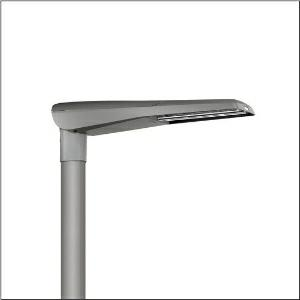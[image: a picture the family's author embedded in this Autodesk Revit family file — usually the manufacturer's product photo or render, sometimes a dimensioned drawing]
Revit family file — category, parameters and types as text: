
# Revit family: streetlight_sl_11_iq_mini___st1_0ab_5xc2nc1f08ge_aec6
name_source: partatom
category: Lighting Fixtures
units: mm (PartAtom-declared; Revit-internal decimal feet)

## family parameters
Cut with Voids When Loaded = No
Host = Face
Light Source = No
Part Type = Normal
Room Calculation Point = No
Round Connector Dimension = Use Diameter
Shared = No

## types (1)
- --- (1 x LED, 2430 lm, 25.3 W, 2200K)
    Apparent Load = 25 VA
    CIE Flux Codes = 29 63 95 100 100
    Color Rendering = 70
    Color Temperature = 2200K
    Default Elevation = 1800 mm
    Description = Streetlight SL 11 iQ mini, mast luminaire, primary light control with 3 zone facetted reflector, of plastic, silver coated, highly specular, primary optical cover: cover, of PMMA, transparent, light distribution: ST1.0aB, light emission: direct distribution, primary light characteristic: asymmetric, installation type: post-top, side-entry, LED, High Power LED, rated luminous flux: 3.010lm, luminous efficacy: 121lm/W, light colour: 722/727/730/740, colour temperature: 2200/2700/3000/4000K, control gear: iQ Street-Remote, control: Street-Remote, Auto-Match, Temp-Guard, Lumen-Switch, Night-Set, Smart-Wire, Light-Fading, Desk-Remote (wireless, voltage-free reading and setting of iQ features in the workshop via application-optimized NFC function/RFID function), optimised constant luminous flux control (CLO 2.0), with cable H07RN-F 5x 1.5mm², mains connection: 230..240V, AC, 50/60Hz, connection cable pre-assembled, cable length: 6,5m, start of lifetime: 25W, end of service life: 26W, reduction: 13W, luminaire housing, of diecast aluminium, powder-coated, Siteco® metallic grey (DB 702S), please order mast flange separately, inclination adjustable without tools: 0°, 5°, 10°, 15° (post-top) | 0°, -5°, -10°, -15° (side-entry), sealing non-destructively replaceable, multi-level sealing system, length: 736mm, width: 174mm, height: 116mm, mast flange for spigot size: 42mm (side-entry): 5XC10008XM4, 60/48mm (side-entry/post-top): 5XC10108XM2, 76/60mm (side-entry/post-top): 5XC10108XM1, mounting height: 4..8m, equipment: standard, protection rating (complete): IP66, insulation class (complete): insulation class II (safety insulation), certification: CE, ENEC, VDE, impact resistance: IK09, permissible operating ambient temperature for outdoor applications: -25..+50°C, standard-compliant lighting for roads and squares, Environmental Product Declaration (EPD) tested and certified by an independent institute, packaging unit: 1 piece

Light Distribution: ST1.0aB
    Height = 116 mm
    Lamp = 1 x LED
    Lamp Light Flux = 2430 lm
    Lamp Power = 25.3 W
    Lamp count = 1
    Length = 736 mm
    Luminous efficacy = 96 lm/W
    Manufacturer = Siteco
    ModVariant = No
    Model = 5XC2NC1F08GE
    Number of Poles = 1
    OnlyDefault = Yes
    Power Factor = 1
    Product Name = Streetlight SL 11 iQ mini | ST1.0aB
    Product group = mast luminaire | pylon top
    ProductGroupID = 6100
    Protection Class = Protection class II
    Protection Degree = IP 66
    RLX_Detail_Level = 1
    RLX_Emergency_Light_Flux = 0 lm
    RLX_Emergency_Type = 0
    RLX_Emergency_Type_DB = No
    RlxData = <blob elided: 34709 chars, md5=1d072d76>
    Socket = socket
    Standby Power = 0 W
    System Light Flux = 2430 lm
    System Power = 25 W
    Type Comments = individual setting: luminous flux: 100 % | dim-lin: 254 | 351 mA
    Type Image = l_1003508.jpg
    URL = http://relux.com
    VarID = @adj_001719
    Voltage = 0 V
    Weight = 0.00 kg
    Width = 174 mm

## geometry (parser evidence)
native form markers: Blend x4, Sweep x9
no freeform markers — native parametric forms only
